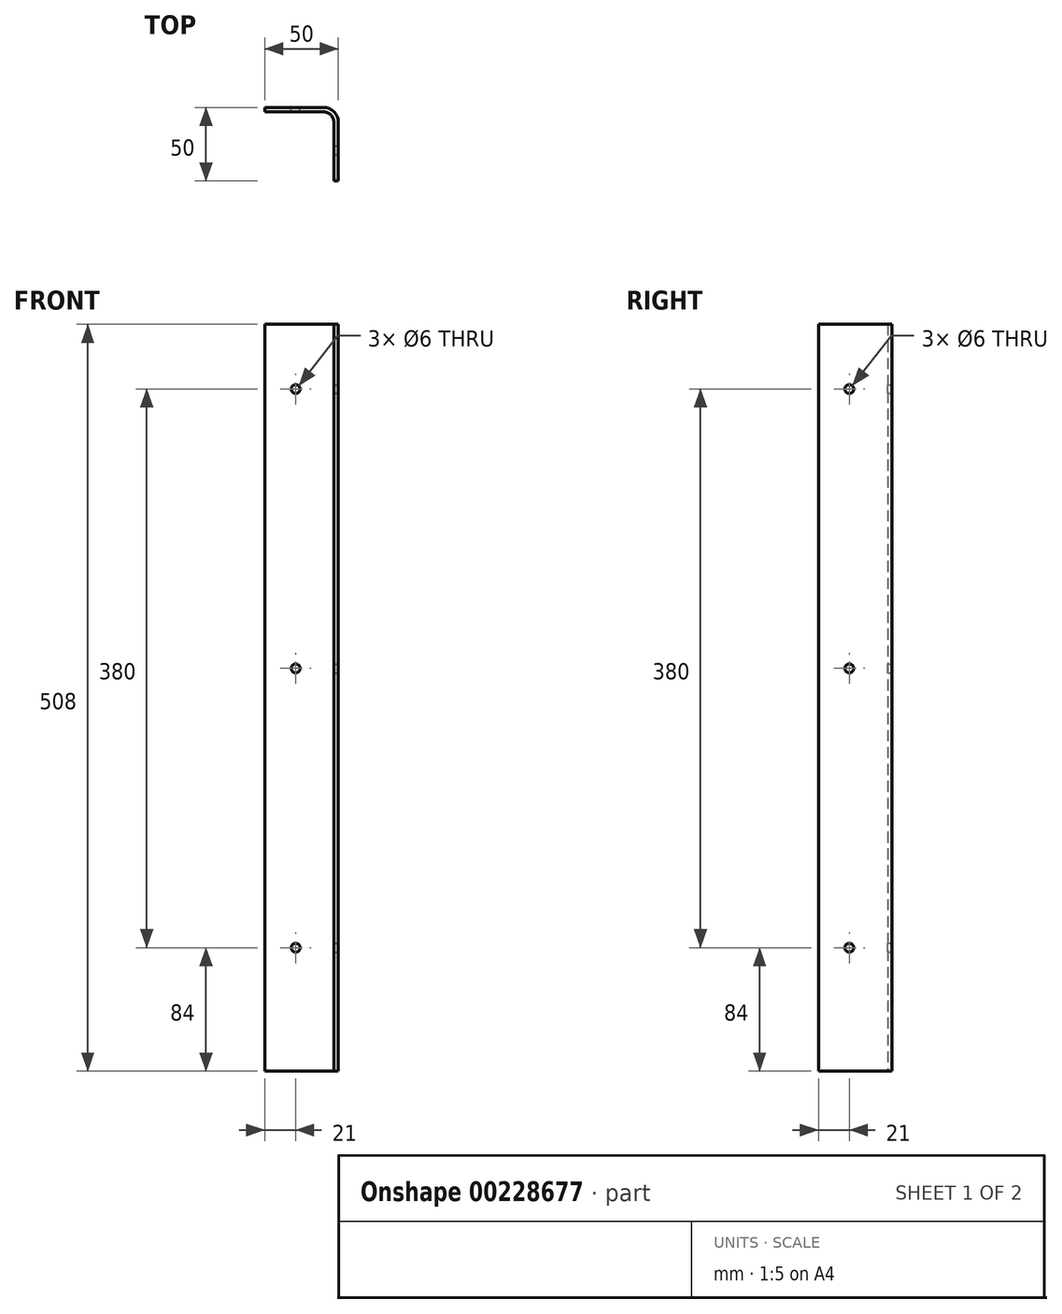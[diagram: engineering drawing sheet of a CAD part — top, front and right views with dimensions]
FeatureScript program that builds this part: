
annotation { "Feature Type Name" : "Feature", "Feature Type Description" : "" }
export const myFeature = defineFeature(function(context is Context, id is Id, definition is map)
    precondition{}
    {
        {
            var Q0;
            Q0=qCreatedBy(makeId("Top.planeOp"),FACE);
            var sketch = newSketch(context, id + "F0", { "sketchPlane" : qUnion([Q0])});
            skLineSegment(sketch, "E0", {"start": v(0, 0) * mm, "end": v(40, 0) * mm});
            skLineSegment(sketch, "E1", {"start": v(50, -10) * mm, "end": v(50, -50) * mm});
            skLineSegment(sketch, "E2", {"start": v(50, -50) * mm, "end": v(47, -50) * mm});
            skLineSegment(sketch, "E3", {"start": v(47, -50) * mm, "end": v(47, -10) * mm});
            skLineSegment(sketch, "E4", {"start": v(40, -3) * mm, "end": v(0, -3) * mm});
            skLineSegment(sketch, "E5", {"start": v(0, -3) * mm, "end": v(0, 0) * mm});
            skPoint(sketch, "E6.visualSharp", {"position": v(50, 0) * mm});
            skArc(sketch, "E6.filletArc", {"start": v(50, -10) * mm, "mid": v(47.07, -2.93) * mm, "end": v(40, 0) * mm});
            skPoint(sketch, "E7.visualSharp", {"position": v(47, -3) * mm});
            skArc(sketch, "E7.filletArc", {"start": v(47, -10) * mm, "mid": v(44.95, -5.05) * mm, "end": v(40, -3) * mm});
            skSolve(sketch);
        }
        {
            var Q0;
            Q0 = qSketchRegion(id + "F0", true);
            extrude(context, id + "F1", {"entities" : qUnion([Q0]), "depth" : (20 * 25.4) * mm});
        }
        {
            var Q0;
            Q0=makeQuery(id+"F1.opExtrude","SWEPT_FACE",FACE,{"disambiguationData":[OSD([sQuery(id+"F0.wireOp",EDGE,"E0")])]});
            var sketch = newSketch(context, id + "F2", { "sketchPlane" : qUnion([Q0])});
            skCircle(sketch, "E8", {"center": v(-21, 464) * mm, "radius": 3 * mm});
            skCircle(sketch, "E9", {"center": v(-21, 274) * mm, "radius": 3 * mm});
            skCircle(sketch, "E10", {"center": v(-21, 84) * mm, "radius": 3 * mm});
            skSolve(sketch);
        }
        {
            var Q0;
            Q0 = qSketchRegion(id + "F2", true);
            extrude(context, id + "F3", {"entities" : qUnion([Q0]), "operationType" : NewBodyOperationType.REMOVE, "endBound" : BoundingType.THROUGH_ALL, "oppositeDirection" : true, "depth" : 25 * mm});
        }
        {
            var Q0;
            Q0=makeQuery(id+"F1.opExtrude","SWEPT_FACE",FACE,{"disambiguationData":[OSD([sQuery(id+"F0.wireOp",EDGE,"E1")])]});
            var sketch = newSketch(context, id + "F4", { "sketchPlane" : qUnion([Q0])});
            skCircle(sketch, "E11", {"center": v(-29, 464) * mm, "radius": 3 * mm});
            skCircle(sketch, "E12", {"center": v(-29, 274) * mm, "radius": 3 * mm});
            skCircle(sketch, "E13", {"center": v(-29, 84) * mm, "radius": 3 * mm});
            skSolve(sketch);
        }
        {
            var Q0;
            Q0 = qSketchRegion(id + "F4", true);
            extrude(context, id + "F5", {"entities" : qUnion([Q0]), "operationType" : NewBodyOperationType.REMOVE, "endBound" : BoundingType.THROUGH_ALL, "oppositeDirection" : true, "depth" : 25 * mm});
        }
    });
